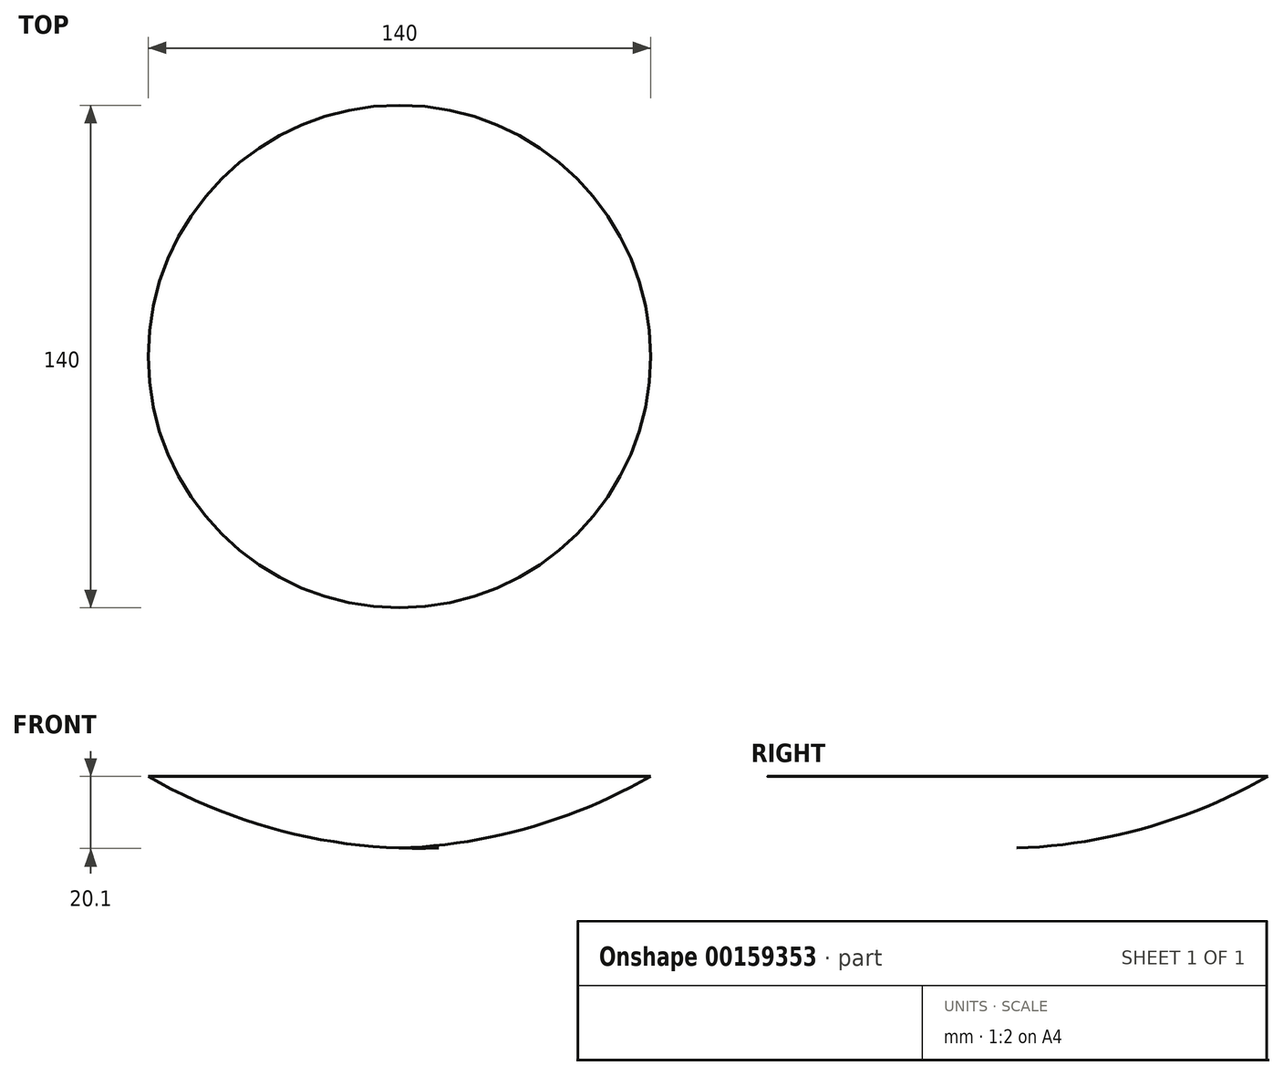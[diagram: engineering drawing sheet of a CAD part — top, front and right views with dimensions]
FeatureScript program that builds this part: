
annotation { "Feature Type Name" : "Feature", "Feature Type Description" : "" }
export const myFeature = defineFeature(function(context is Context, id is Id, definition is map)
    precondition{}
    {
        {
            var Q0;
            Q0=qCreatedBy(makeId("Front.planeOp"),FACE);
            var sketch = newSketch(context, id + "F0", { "sketchPlane" : qUnion([Q0])});
            skLineSegment(sketch, "E0", {"start": v(0, 0) * mm, "end": v(70, 0) * mm});
            skLineSegment(sketch, "E1", {"start": v(0, 0) * mm, "end": v(0, -20) * mm});
            skArc(sketch, "E2", {"start": v(0, -20) * mm, "mid": v(36.22, -14.26) * mm, "end": v(70, 0) * mm});
            skSolve(sketch);
        }
        {
            var Q0;
            Q0 = qSketchRegion(id + "F0", true);
            var Q1;
            Q1=sQuery(id+"F0.wireOp",EDGE,"E1");
            revolve(context, id + "F1", {"entities" : qUnion([Q0]), "axis" : qUnion([Q1]), "revolveType" : RevolveType.FULL});
        }
    });
